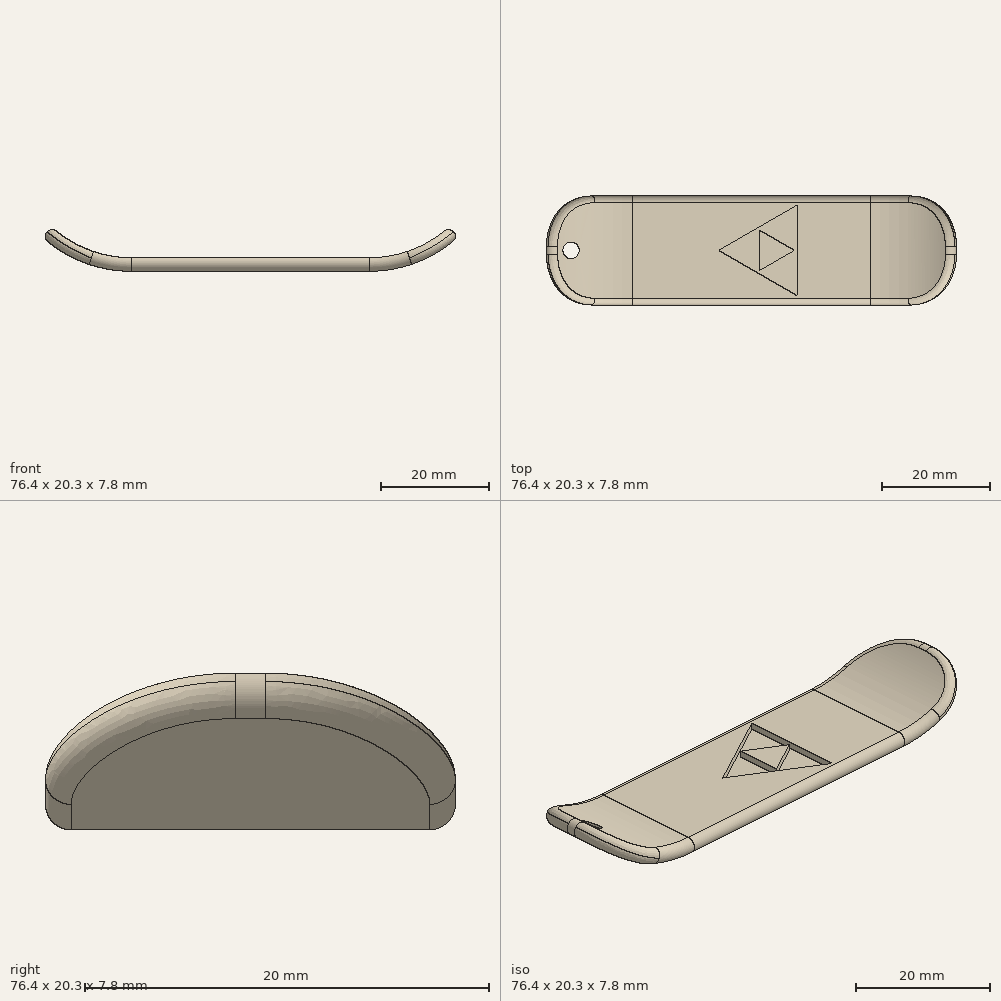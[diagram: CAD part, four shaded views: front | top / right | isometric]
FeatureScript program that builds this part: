
annotation { "Feature Type Name" : "Feature", "Feature Type Description" : "" }
export const myFeature = defineFeature(function(context is Context, id is Id, definition is map)
    precondition{}
    {
        {
            var Q0;
            Q0=qCreatedBy(makeId("Front.planeOp"),FACE);
            var sketch = newSketch(context, id + "F0", { "sketchPlane" : qUnion([Q0])});
            skLineSegment(sketch, "E0", {"start": v(-22.22, 0) * mm, "end": v(22.22, 0) * mm});
            skArc(sketch, "E1", {"start": v(-38.73, 6.39) * mm, "mid": v(-31.08, 1.65) * mm, "end": v(-22.22, 0) * mm});
            skArc(sketch, "E2.MirrorCS", {"start": v(38.73, 6.39) * mm, "mid": v(31.08, 1.65) * mm, "end": v(22.23, 0) * mm});
            skArc(sketch, "E3.0", {"start": v(37.03, 8.27) * mm, "mid": v(30.16, 4.02) * mm, "end": v(22.22, 2.54) * mm});
            skLineSegment(sketch, "E3.1", {"start": v(-22.22, 2.54) * mm, "end": v(22.22, 2.54) * mm});
            skArc(sketch, "E3.2", {"start": v(-37.03, 8.27) * mm, "mid": v(-30.16, 4.02) * mm, "end": v(-22.22, 2.54) * mm});
            skLineSegment(sketch, "E4", {"start": v(-38.73, 6.39) * mm, "end": v(-37.03, 8.27) * mm});
            skLineSegment(sketch, "E5", {"start": v(37.03, 8.27) * mm, "end": v(38.73, 6.39) * mm});
            skSolve(sketch);
        }
        {
            var Q0;
            Q0 = qSketchRegion(id + "F0", true);
            extrude(context, id + "F1", {"entities" : qUnion([Q0]), "endBound" : BoundingType.SYMMETRIC, "depth" : 20.32 * mm});
        }
        {
            var Q0;
            Q0=makeQuery(id+"F1.opExtrude","CAP_EDGE",EDGE,{"disambiguationData":[OSD([sQuery(id+"F0.wireOp",EDGE,"E4")])],"isStart":false});
            var Q1;
            Q1=makeQuery(id+"F1.opExtrude","CAP_EDGE",EDGE,{"disambiguationData":[OSD([sQuery(id+"F0.wireOp",EDGE,"E4")])],"isStart":true});
            var Q2;
            Q2=makeQuery(id+"F1.opExtrude","CAP_EDGE",EDGE,{"disambiguationData":[OSD([sQuery(id+"F0.wireOp",EDGE,"E5")])],"isStart":true});
            var Q3;
            Q3=makeQuery(id+"F1.opExtrude","CAP_EDGE",EDGE,{"disambiguationData":[OSD([sQuery(id+"F0.wireOp",EDGE,"E5")])],"isStart":false});
            fillet(context, id + "F2", {"entities" : qUnion([Q0, Q1, Q2, Q3]), "radius" : 9.4 * mm, "tangentPropagation" : true, "allowEdgeOverflow" : false});
        }
        {
            var Q0;
            Q0=makeQuery(id+"F1.opExtrude","CAP_EDGE",EDGE,{"disambiguationData":[OSD([sQuery(id+"F0.wireOp",EDGE,"E3.2")])],"isStart":false});
            var Q1;
            Q1=makeQuery(id+"F2.opFillet","BLEND_EDGE",EDGE,{"blendedFrom":[makeQuery(id+"F1.opExtrude","CAP_EDGE",EDGE,{"disambiguationData":[OSD([sQuery(id+"F0.wireOp",EDGE,"E4")])],"isStart":false}),makeQuery(id+"F1.opExtrude","SWEPT_FACE",FACE,{"disambiguationData":[OSD([sQuery(id+"F0.wireOp",EDGE,"E1")])]})],"blendedInto":[makeQuery(id+"F1.opExtrude","SWEPT_FACE",FACE,{"disambiguationData":[OSD([sQuery(id+"F0.wireOp",EDGE,"E1")])]})]});
            fillet(context, id + "F3", {"entities" : qUnion([Q0, Q1]), "radius" : 1.27 * mm, "tangentPropagation" : true, "allowEdgeOverflow" : false});
        }
        {
            var Q0;
            Q0=qCreatedBy(makeId("Top.planeOp"),FACE);
            var sketch = newSketch(context, id + "F4", { "sketchPlane" : qUnion([Q0])});
            skPoint(sketch, "E6.0", {"position": v(-38.18, 0.76) * mm});
            skCircle(sketch, "E7", {"center": v(-33.61, 0) * mm, "radius": 1.52 * mm});
            skSolve(sketch);
        }
        {
            var Q0;
            Q0 = qSketchRegion(id + "F4", true);
            extrude(context, id + "F5", {"entities" : qUnion([Q0]), "operationType" : NewBodyOperationType.REMOVE, "depth" : 25.4 * mm});
        }
        {
            var Q0;
            Q0=makeQuery(id+"F1.opExtrude","SWEPT_FACE",FACE,{"disambiguationData":[OSD([sQuery(id+"F0.wireOp",EDGE,"E3.1")])]});
            var sketch = newSketch(context, id + "F6", { "sketchPlane" : qUnion([Q0])});
            skLineSegment(sketch, "E8", {"start": v(8.8, -8.9) * mm, "end": v(8.8, 8.9) * mm, "construction": true});
            skLineSegment(sketch, "E9", {"start": v(8.8, 8.9) * mm, "end": v(-6.59, 0) * mm, "construction": true});
            skLineSegment(sketch, "E10", {"start": v(-6.59, 0) * mm, "end": v(8.8, -8.9) * mm, "construction": true});
            skLineSegment(sketch, "E11.0", {"start": v(8.55, -8.45) * mm, "end": v(8.55, 8.45) * mm});
            skLineSegment(sketch, "E11.1", {"start": v(-6.08, 0) * mm, "end": v(8.55, -8.45) * mm});
            skLineSegment(sketch, "E11.2", {"start": v(8.55, 8.45) * mm, "end": v(-6.08, 0) * mm});
            skLineSegment(sketch, "E12", {"start": v(1.24, -4.23) * mm, "end": v(8.55, 0) * mm, "construction": true});
            skLineSegment(sketch, "E13", {"start": v(8.55, 0) * mm, "end": v(1.24, 4.23) * mm, "construction": true});
            skLineSegment(sketch, "E14", {"start": v(1.24, 4.23) * mm, "end": v(1.24, -4.23) * mm, "construction": true});
            skLineSegment(sketch, "E15.0", {"start": v(1.5, 3.79) * mm, "end": v(1.5, -3.79) * mm});
            skLineSegment(sketch, "E15.1", {"start": v(8.05, 0) * mm, "end": v(1.5, 3.79) * mm});
            skLineSegment(sketch, "E15.2", {"start": v(1.5, -3.79) * mm, "end": v(8.05, 0) * mm});
            skSolve(sketch);
        }
        {
            var Q0;
            Q0=makeQuery(id+"F6.imprint","IMPRINT",FACE,{"disambiguationData":[TD([[makeQuery(id+"F6.imprint","IMPRINT",EDGE,{"derivedFrom":sQuery(id+"F6.wireOp",EDGE,"E11.0")}),1.0]])]});
            extrude(context, id + "F7", {"entities" : qUnion([Q0]), "operationType" : NewBodyOperationType.REMOVE, "oppositeDirection" : true, "depth" : 1.02 * mm});
        }
    });
